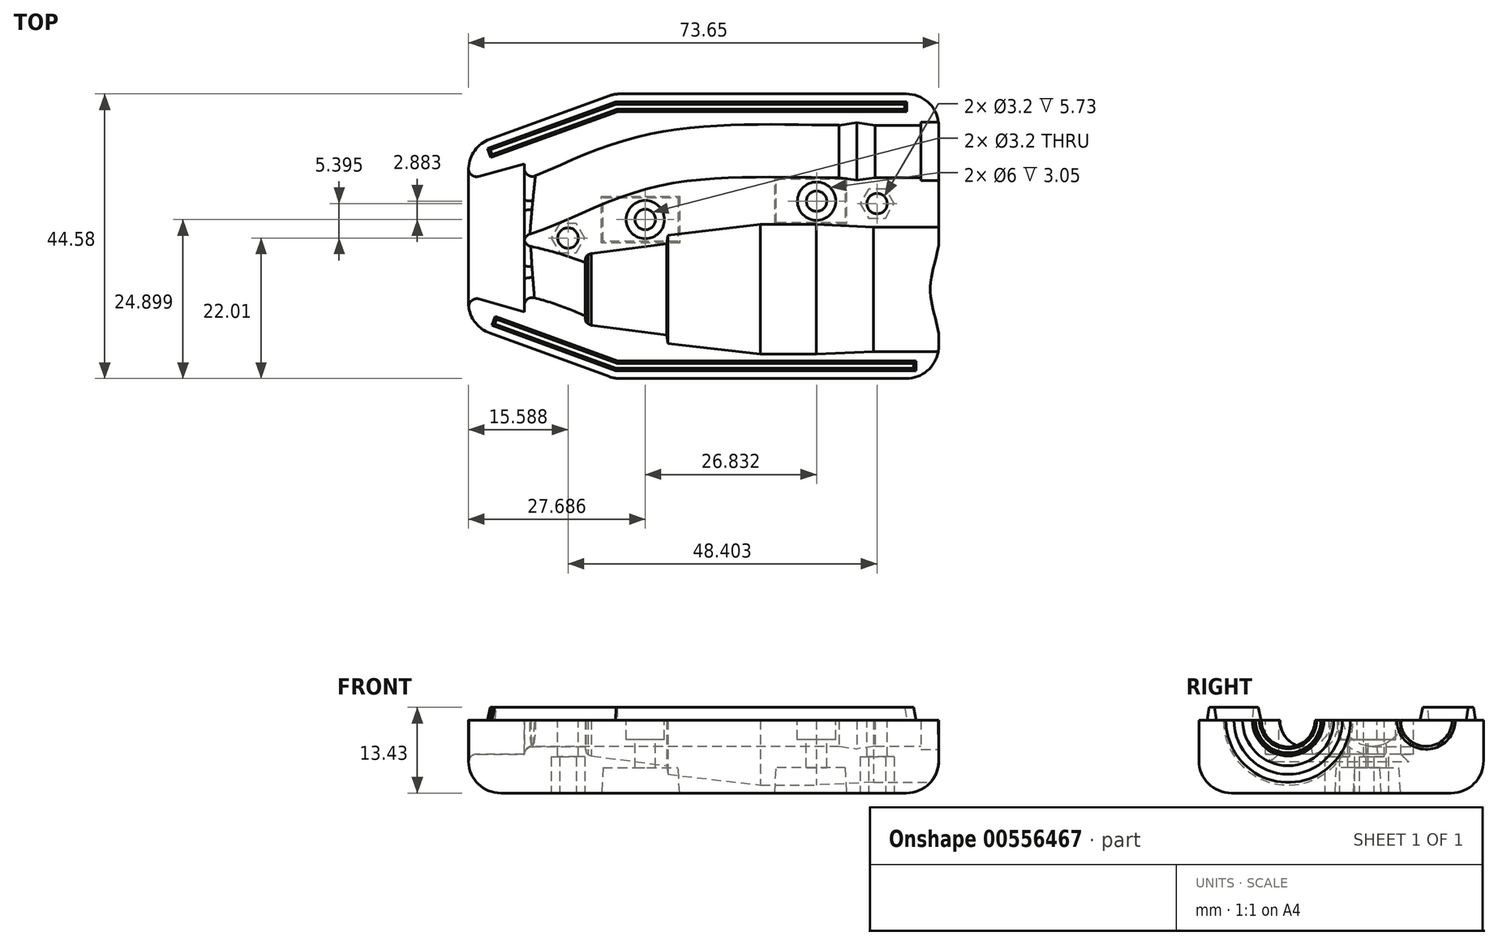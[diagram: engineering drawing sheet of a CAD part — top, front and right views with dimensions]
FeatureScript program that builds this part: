
annotation { "Feature Type Name" : "Feature", "Feature Type Description" : "" }
export const myFeature = defineFeature(function(context is Context, id is Id, definition is map)
    precondition{}
    {
        {
            var Q0;
            Q0=qCreatedBy(makeId("Top.planeOp"),FACE);
            var sketch = newSketch(context, id + "F0", { "sketchPlane" : qUnion([Q0])});
            skLineSegment(sketch, "E0", {"start": v(-29.16, 2.44) * mm, "end": v(45.25, 2.44) * mm});
            skLineSegment(sketch, "E1", {"start": v(45.25, 2.44) * mm, "end": v(45.25, -7.31) * mm});
            skLineSegment(sketch, "E2", {"start": v(45.25, -7.31) * mm, "end": v(33.01, -7.3) * mm});
            skLineSegment(sketch, "E3", {"start": v(33.01, -7.3) * mm, "end": v(31, -7.31) * mm});
            skLineSegment(sketch, "E4", {"start": v(31, -7.31) * mm, "end": v(16, -7.31) * mm});
            skLineSegment(sketch, "E5", {"start": v(16, -7.31) * mm, "end": v(7, -7.72) * mm});
            skLineSegment(sketch, "E6", {"start": v(7, -7.72) * mm, "end": v(-1.71, -7.72) * mm});
            skLineSegment(sketch, "E7", {"start": v(-1.71, -7.72) * mm, "end": v(-16.21, -6.04) * mm});
            skLineSegment(sketch, "E8", {"start": v(-16.21, -6.04) * mm, "end": v(-16.37, -4.7) * mm});
            skLineSegment(sketch, "E9", {"start": v(-16.37, -4.7) * mm, "end": v(-28.19, -3.17) * mm});
            skLineSegment(sketch, "E10", {"start": v(-28.19, -3.17) * mm, "end": v(-28.73, -2.96) * mm});
            skLineSegment(sketch, "E11", {"start": v(-28.73, -2.96) * mm, "end": v(-29.03, -2.68) * mm});
            skLineSegment(sketch, "E12", {"start": v(-29.03, -2.68) * mm, "end": v(-29.18, -2.06) * mm});
            skLineSegment(sketch, "E13", {"start": v(-29.18, -2.06) * mm, "end": v(-29.16, 2.44) * mm});
            skLineSegment(sketch, "E14.top", {"start": v(29.2, 18.83) * mm, "end": v(41.5, 18.83) * mm});
            skLineSegment(sketch, "E14.right", {"start": v(41.5, 24.03) * mm, "end": v(41.5, 18.83) * mm});
            skLineSegment(sketch, "E15", {"start": v(29.2, 19.46) * mm, "end": v(23.4, 19.46) * mm});
            skLineSegment(sketch, "E16", {"start": v(23.4, 19.46) * mm, "end": v(23.4, 24.03) * mm});
            skLineSegment(sketch, "E17", {"start": v(41.5, 24.03) * mm, "end": v(23.4, 24.03) * mm});
            skLineSegment(sketch, "E18", {"start": v(29.2, 18.83) * mm, "end": v(29.2, 19.46) * mm});
            skLineSegment(sketch, "E19.MirrorCS", {"start": v(-28.73, 7.85) * mm, "end": v(-29.03, 7.56) * mm});
            skLineSegment(sketch, "E20.MirrorCS", {"start": v(-29.03, 7.56) * mm, "end": v(-29.18, 6.94) * mm});
            skLineSegment(sketch, "E21.MirrorCS", {"start": v(33.01, 12.2) * mm, "end": v(31, 12.2) * mm});
            skLineSegment(sketch, "E22.MirrorCS", {"start": v(-28.19, 8.06) * mm, "end": v(-28.73, 7.85) * mm});
            skLineSegment(sketch, "E23.MirrorCS", {"start": v(-16.21, 10.93) * mm, "end": v(-16.37, 9.58) * mm});
            skLineSegment(sketch, "E24.MirrorCS", {"start": v(-16.37, 9.58) * mm, "end": v(-28.19, 8.06) * mm});
            skLineSegment(sketch, "E25.MirrorCS", {"start": v(7, 12.6) * mm, "end": v(-1.71, 12.6) * mm});
            skLineSegment(sketch, "E26.MirrorCS", {"start": v(45.25, 12.2) * mm, "end": v(33.01, 12.2) * mm});
            skLineSegment(sketch, "E27.MirrorCS", {"start": v(-1.71, 12.6) * mm, "end": v(-16.21, 10.93) * mm});
            skLineSegment(sketch, "E28.MirrorCS", {"start": v(16, 12.2) * mm, "end": v(7, 12.6) * mm});
            skLineSegment(sketch, "E29.MirrorCS", {"start": v(31, 12.2) * mm, "end": v(16, 12.2) * mm});
            skLineSegment(sketch, "E30.MirrorCS", {"start": v(45.25, 2.44) * mm, "end": v(45.25, 12.2) * mm});
            skLineSegment(sketch, "E31.MirrorCS", {"start": v(-29.18, 6.94) * mm, "end": v(-29.16, 2.44) * mm});
            skLineSegment(sketch, "E32", {"start": v(41.5, 20.03) * mm, "end": v(44.1, 20.03) * mm});
            skLineSegment(sketch, "E33", {"start": v(44.1, 20.03) * mm, "end": v(44.1, 24.03) * mm});
            skLineSegment(sketch, "E34", {"start": v(44.1, 24.03) * mm, "end": v(41.5, 24.03) * mm});
            skLineSegment(sketch, "E35", {"start": v(44.1, 20.03) * mm, "end": v(44.1, 19.46) * mm});
            skLineSegment(sketch, "E36", {"start": v(44.1, 19.46) * mm, "end": v(45.25, 19.46) * mm});
            skLineSegment(sketch, "E37", {"start": v(45.25, 19.46) * mm, "end": v(45.32, 24.03) * mm});
            skLineSegment(sketch, "E38", {"start": v(45.32, 24.03) * mm, "end": v(44.1, 24.03) * mm});
            skLineSegment(sketch, "E39", {"start": v(23.4, 24.03) * mm, "end": v(16.2, 24.03) * mm});
            skLineSegment(sketch, "E40", {"start": v(16.2, 24.03) * mm, "end": v(16.2, 19.93) * mm});
            skLineSegment(sketch, "E41", {"start": v(16.2, 19.93) * mm, "end": v(23.4, 19.93) * mm});
            skLineSegment(sketch, "E42", {"start": v(16.2, 19.93) * mm, "end": v(13.4, 19.53) * mm});
            skLineSegment(sketch, "E43", {"start": v(13.4, 19.53) * mm, "end": v(10.6, 19.93) * mm});
            skLineSegment(sketch, "E44", {"start": v(10.6, 19.93) * mm, "end": v(10.6, 24.03) * mm});
            skLineSegment(sketch, "E45", {"start": v(10.6, 24.03) * mm, "end": v(16.2, 24.03) * mm});
            skLineSegment(sketch, "E46.MirrorCS", {"start": v(44.1, 28.03) * mm, "end": v(44.1, 28.6) * mm});
            skLineSegment(sketch, "E47.MirrorCS", {"start": v(44.1, 28.6) * mm, "end": v(45.25, 28.6) * mm});
            skLineSegment(sketch, "E48.MirrorCS", {"start": v(29.2, 29.24) * mm, "end": v(29.2, 28.6) * mm});
            skLineSegment(sketch, "E49.MirrorCS", {"start": v(44.1, 28.03) * mm, "end": v(44.1, 24.03) * mm});
            skLineSegment(sketch, "E50.MirrorCS", {"start": v(16.2, 24.03) * mm, "end": v(16.2, 28.13) * mm});
            skLineSegment(sketch, "E51.MirrorCS", {"start": v(23.4, 28.6) * mm, "end": v(23.4, 24.03) * mm});
            skLineSegment(sketch, "E52.MirrorCS", {"start": v(10.6, 28.13) * mm, "end": v(10.6, 24.03) * mm});
            skLineSegment(sketch, "E53.MirrorCS", {"start": v(29.2, 28.6) * mm, "end": v(23.4, 28.6) * mm});
            skLineSegment(sketch, "E54.MirrorCS", {"start": v(41.5, 24.03) * mm, "end": v(41.5, 29.24) * mm});
            skLineSegment(sketch, "E55.MirrorCS", {"start": v(29.2, 29.24) * mm, "end": v(41.5, 29.24) * mm});
            skLineSegment(sketch, "E56.MirrorCS", {"start": v(45.25, 28.6) * mm, "end": v(45.32, 24.03) * mm});
            skLineSegment(sketch, "E57.MirrorCS", {"start": v(13.4, 28.53) * mm, "end": v(10.6, 28.13) * mm});
            skLineSegment(sketch, "E58.MirrorCS", {"start": v(41.5, 28.03) * mm, "end": v(44.1, 28.03) * mm});
            skLineSegment(sketch, "E59.MirrorCS", {"start": v(16.2, 28.13) * mm, "end": v(13.4, 28.53) * mm});
            skLineSegment(sketch, "E60.MirrorCS", {"start": v(16.2, 28.13) * mm, "end": v(23.4, 28.13) * mm});
            skSolve(sketch);
        }
        {
            var Q0;
            Q0=qCreatedBy(makeId("Top.planeOp"),FACE);
            var sketch = newSketch(context, id + "F1", { "sketchPlane" : qUnion([Q0])});
            skLineSegment(sketch, "E61.0", {"start": v(45.25, 2.44) * mm, "end": v(45.25, -7.31) * mm});
            skLineSegment(sketch, "E62", {"start": v(26.2, 33.05) * mm, "end": v(26.2, -11.53) * mm});
            skLineSegment(sketch, "E63", {"start": v(26.2, -11.53) * mm, "end": v(-24.6, -11.53) * mm});
            skLineSegment(sketch, "E64", {"start": v(-24.6, -11.53) * mm, "end": v(-47.46, -3.2) * mm});
            skLineSegment(sketch, "E65", {"start": v(-47.46, -3.2) * mm, "end": v(-47.46, 24.73) * mm});
            skLineSegment(sketch, "E66", {"start": v(-47.46, 24.73) * mm, "end": v(-24.6, 33.05) * mm});
            skLineSegment(sketch, "E67", {"start": v(-24.6, 33.05) * mm, "end": v(26.2, 33.05) * mm});
            skLineSegment(sketch, "E68.0", {"start": v(29.2, 29.24) * mm, "end": v(41.5, 29.24) * mm});
            skSolve(sketch);
        }
        {
            var Q0;
            Q0=qSketchRegion(id+"F1",true);
            extrude(context, id + "F2", {"entities" : qUnion([Q0]), "oppositeDirection" : true, "depth" : 11.43 * mm, "offsetDistance" : 25.4 * mm});
        }
        {
            var Q0;
            Q0=makeQuery(id+"F0.imprint","IMPRINT",FACE,{"disambiguationData":[TD([[makeQuery(id+"F0.imprint","IMPRINT",EDGE,{"derivedFrom":sQuery(id+"F0.wireOp",EDGE,"E0")}),-1.0]])]});
            var Q1;
            Q1=sQuery(id+"F0.wireOp",EDGE,"E0");
            revolve(context, id + "F3", {"operationType" : NewBodyOperationType.REMOVE, "entities" : qUnion([Q0]), "axis" : qUnion([Q1]), "revolveType" : RevolveType.FULL, "oppositeDirection" : true});
        }
        {
            var Q0;
            Q0=makeQuery(id+"F0.imprint","IMPRINT",FACE,{"disambiguationData":[TD([[makeQuery(id+"F0.imprint","IMPRINT",EDGE,{"derivedFrom":sQuery(id+"F0.wireOp",EDGE,"E14.top")}),1.0]])]});
            var Q1;
            Q1=makeQuery(id+"F0.imprint","IMPRINT",FACE,{"disambiguationData":[TD([[makeQuery(id+"F0.imprint","IMPRINT",EDGE,{"derivedFrom":sQuery(id+"F0.wireOp",EDGE,"E40")}),1.0]])]});
            var Q2;
            Q2=makeQuery(id+"F0.imprint","IMPRINT",FACE,{"disambiguationData":[TD([[makeQuery(id+"F0.imprint","IMPRINT",EDGE,{"derivedFrom":sQuery(id+"F0.wireOp",EDGE,"E40")}),-1.0]])]});
            var Q3;
            Q3=sQuery(id+"F0.wireOp",EDGE,"E17");
            revolve(context, id + "F4", {"operationType" : NewBodyOperationType.REMOVE, "entities" : qUnion([Q0, Q1, Q2]), "axis" : qUnion([Q3]), "revolveType" : RevolveType.FULL});
        }
        {
            var Q0;
            Q0=makeQuery(id+"F2.opExtrude","CAP_FACE",FACE,{"disambiguationData":[OSD([sQuery(id+"F1.wireOp",EDGE,"FN9DgEXL-DUnT-EqR8-ggIH-wTex11pTKOJ6"),sQuery(id+"F1.wireOp",EDGE,"Mmaicck8-LA38-ALDy-QV3c-pMFCgAv4KP83"),sQuery(id+"F1.wireOp",EDGE,"E62"),sQuery(id+"F1.wireOp",EDGE,"E63"),sQuery(id+"F1.wireOp",EDGE,"E64"),sQuery(id+"F1.wireOp",EDGE,"E65"),sQuery(id+"F1.wireOp",EDGE,"E66"),sQuery(id+"F1.wireOp",EDGE,"E67")])],"isStart":true});
            var sketch = newSketch(context, id + "F5", { "sketchPlane" : qUnion([Q0])});
            skLineSegment(sketch, "E69.0", {"start": v(-29.16, 2.44) * mm, "end": v(45.25, 2.44) * mm});
            skFitSpline(sketch, "E70", {"points": [v(-29.16, 2.44) * mm, v(-47.46, 6.7) * mm, v(-83.77, 9.93) * mm], "startDerivative": vector(-48.46, 20.5) * mm, "endDerivative": vector(-77.25, 2.74) * mm});
            skSolve(sketch);
        }
        {
            var Q0;
            Q0=sQuery(id+"F5.wireOp",VERTEX,"E70.0.internal");
            var Q1;
            Q1=sQuery(id+"F5.wireOp",EDGE,"E69.0");
            cPlane(context, id + "F6", {"entities" : qUnion([Q0, Q1]), "cplaneType" : CPlaneType.LINE_POINT, "offset" : 25.4 * mm, "width" : 152.4 * mm, "height" : 152.4 * mm});
        }
        {
            var Q0;
            Q0=qCreatedBy(id+"F6.planeOp",FACE);
            var sketch = newSketch(context, id + "F7", { "sketchPlane" : qUnion([Q0])});
            skCircle(sketch, "E71", {"center": v(2.44, 0) * mm, "radius": 4.2 * mm});
            skSolve(sketch);
        }
        {
            var Q0;
            Q0=qSketchRegion(id+"F7",true);
            var Q1;
            Q1=sQuery(id+"F5.wireOp",EDGE,"E70");
            sweep(context, id + "F8", {"operationType" : NewBodyOperationType.REMOVE, "profiles" : qUnion([Q0]), "path" : qUnion([Q1])});
        }
        {
            var Q0;
            Q0=sQuery(id+"F0.wireOp",VERTEX,"E45.start");
            var Q1;
            Q1=sQuery(id+"F0.wireOp",EDGE,"E45");
            cPlane(context, id + "F9", {"entities" : qUnion([Q0, Q1]), "cplaneType" : CPlaneType.LINE_POINT, "offset" : 25.4 * mm, "width" : 152.4 * mm, "height" : 152.4 * mm});
        }
        {
            var Q0;
            {var subQ0=sQuery(id+"F1.wireOp",EDGE,"E62");var subQ1=sQuery(id+"F1.wireOp",EDGE,"E65");var subQ2=sQuery(id+"F1.wireOp",EDGE,"E66");var subQ3=sQuery(id+"F1.wireOp",EDGE,"E67");Q0=makeQuery(id+"F8.boolean.opBoolean","SPLIT",FACE,{"disambiguationData":[TD([makeQuery(id+"F2.opExtrude","SWEPT_FACE",FACE,{"disambiguationData":[OSD([subQ2])]})])],"derivedFrom":makeQuery(id+"F2.opExtrude","CAP_FACE",FACE,{"disambiguationData":[OSD([subQ0,sQuery(id+"F1.wireOp",EDGE,"E63"),sQuery(id+"F1.wireOp",EDGE,"E64"),subQ1,subQ2,subQ3])],"isStart":true})});}
            var sketch = newSketch(context, id + "F10", { "sketchPlane" : qUnion([Q0])});
            skLineSegment(sketch, "E72.0", {"start": v(10.6, 24.03) * mm, "end": v(16.2, 24.03) * mm});
            skFitSpline(sketch, "E73", {"points": [v(10.6, 24.03) * mm, v(-17.54, 22.88) * mm, v(-35.92, 16.19) * mm, v(-61.27, 13.83) * mm], "startDerivative": vector(-66.57, 0.28) * mm, "endDerivative": vector(-121.3, 10.88) * mm});
            skSolve(sketch);
        }
        {
            var Q0;
            Q0=qCreatedBy(id+"F9.planeOp",FACE);
            var sketch = newSketch(context, id + "F11", { "sketchPlane" : qUnion([Q0])});
            skCircle(sketch, "E74", {"center": v(24.03, 0) * mm, "radius": 4.12 * mm});
            skSolve(sketch);
        }
        {
            var Q0;
            Q0=qSketchRegion(id+"F11",true);
            var Q1;
            Q1=sQuery(id+"F10.wireOp",EDGE,"E73");
            sweep(context, id + "F12", {"operationType" : NewBodyOperationType.REMOVE, "profiles" : qUnion([Q0]), "path" : qUnion([Q1])});
        }
        {
            var Q0;
            {var subQ4=sQuery(id+"F1.wireOp",EDGE,"E62");var subQ8=makeQuery(id+"F3.boolean.opBoolean","COPY",FACE,{"derivedFrom":makeQuery(id+"F3.opRevolve","SWEPT_FACE",FACE,{"disambiguationData":[OSD([sQuery(id+"F0.wireOp",EDGE,"E4")])]})});var subQ15=sQuery(id+"F1.wireOp",EDGE,"E65");var subQ16=sQuery(id+"F1.wireOp",EDGE,"E66");var subQ17=sQuery(id+"F1.wireOp",EDGE,"E67");Q0=makeQuery(id+"F12.boolean.opBoolean","SPLIT",FACE,{"disambiguationData":[TD([subQ8])],"derivedFrom":makeQuery(id+"F8.boolean.opBoolean","SPLIT",FACE,{"disambiguationData":[TD([makeQuery(id+"F2.opExtrude","SWEPT_FACE",FACE,{"disambiguationData":[OSD([subQ16])]})])],"derivedFrom":makeQuery(id+"F2.opExtrude","CAP_FACE",FACE,{"disambiguationData":[OSD([subQ4,sQuery(id+"F1.wireOp",EDGE,"E63"),sQuery(id+"F1.wireOp",EDGE,"E64"),subQ15,subQ16,subQ17])],"isStart":true})})});}
            var sketch = newSketch(context, id + "F13", { "sketchPlane" : qUnion([Q0])});
            skCircle(sketch, "E75", {"center": v(7.07, 16.25) * mm, "radius": 3 * mm});
            skCircle(sketch, "E76", {"center": v(-19.76, 13.37) * mm, "radius": 3 * mm});
            skSolve(sketch);
        }
        {
            var Q0;
            Q0 = qSketchRegion(id + "F13", true);
            extrude(context, id + "F14", {"entities" : qUnion([Q0]), "operationType" : NewBodyOperationType.REMOVE, "oppositeDirection" : true, "depth" : 3.05 * mm, "offsetDistance" : 25.4 * mm});
        }
        {
            var Q0;
            {var subQ4=sQuery(id+"F1.wireOp",EDGE,"E62");var subQ7=sQuery(id+"F1.wireOp",EDGE,"E65");var subQ8=makeQuery(id+"F2.opExtrude","SWEPT_FACE",FACE,{"disambiguationData":[OSD([subQ7])]});var subQ10=sQuery(id+"F1.wireOp",EDGE,"E66");var subQ11=makeQuery(id+"F2.opExtrude","SWEPT_FACE",FACE,{"disambiguationData":[OSD([subQ10])]});var subQ12=sQuery(id+"F1.wireOp",EDGE,"E67");Q0=makeQuery(id+"F12.boolean.opBoolean","SPLIT",FACE,{"disambiguationData":[TD([subQ8])],"derivedFrom":makeQuery(id+"F8.boolean.opBoolean","SPLIT",FACE,{"disambiguationData":[TD([subQ11])],"derivedFrom":makeQuery(id+"F2.opExtrude","CAP_FACE",FACE,{"disambiguationData":[OSD([subQ4,sQuery(id+"F1.wireOp",EDGE,"E63"),sQuery(id+"F1.wireOp",EDGE,"E64"),subQ7,subQ10,subQ12])],"isStart":true})})});}
            var sketch = newSketch(context, id + "F15", { "sketchPlane" : qUnion([Q0])});
            skLineSegment(sketch, "E77.0", {"start": v(-24.38, 31.8) * mm, "end": v(21.2, 31.8) * mm});
            skLineSegment(sketch, "E77.1", {"start": v(-44.47, 24.49) * mm, "end": v(-24.38, 31.8) * mm});
            skPoint(sketch, "E78", {"position": v(21.2, 31.8) * mm});
            skPoint(sketch, "E79", {"position": v(-44.47, 24.49) * mm});
            skLineSegment(sketch, "E80.0", {"start": v(-24.11, 30.3) * mm, "end": v(21.2, 30.3) * mm});
            skLineSegment(sketch, "E80.1", {"start": v(-43.95, 23.08) * mm, "end": v(-24.11, 30.3) * mm});
            skLineSegment(sketch, "E81", {"start": v(21.2, 30.3) * mm, "end": v(21.2, 31.8) * mm});
            skLineSegment(sketch, "E82", {"start": v(-44.47, 24.49) * mm, "end": v(-43.95, 23.08) * mm});
            skLineSegment(sketch, "E83.0", {"start": v(-24.38, -10.28) * mm, "end": v(-43.8, -3.21) * mm});
            skLineSegment(sketch, "E83.1", {"start": v(22.64, -10.28) * mm, "end": v(-24.38, -10.28) * mm});
            skPoint(sketch, "E84", {"position": v(22.64, -10.28) * mm});
            skPoint(sketch, "E85", {"position": v(-43.8, -3.21) * mm});
            skLineSegment(sketch, "E86.0", {"start": v(-24.11, -8.78) * mm, "end": v(-43.28, -1.8) * mm});
            skLineSegment(sketch, "E86.1", {"start": v(22.64, -8.78) * mm, "end": v(-24.11, -8.78) * mm});
            skLineSegment(sketch, "E87", {"start": v(22.64, -10.28) * mm, "end": v(22.64, -8.78) * mm});
            skLineSegment(sketch, "E88", {"start": v(-43.8, -3.21) * mm, "end": v(-43.28, -1.8) * mm});
            skSolve(sketch);
        }
        {
            var Q0;
            {var subQ4=sQuery(id+"F1.wireOp",EDGE,"E62");var subQ8=makeQuery(id+"F3.boolean.opBoolean","COPY",FACE,{"derivedFrom":makeQuery(id+"F3.opRevolve","SWEPT_FACE",FACE,{"disambiguationData":[OSD([sQuery(id+"F0.wireOp",EDGE,"E4")])]})});var subQ19=sQuery(id+"F1.wireOp",EDGE,"E65");var subQ20=sQuery(id+"F1.wireOp",EDGE,"E66");var subQ21=sQuery(id+"F1.wireOp",EDGE,"E67");Q0=makeQuery(id+"F12.boolean.opBoolean","SPLIT",FACE,{"disambiguationData":[TD([subQ8])],"derivedFrom":makeQuery(id+"F8.boolean.opBoolean","SPLIT",FACE,{"disambiguationData":[TD([makeQuery(id+"F2.opExtrude","SWEPT_FACE",FACE,{"disambiguationData":[OSD([subQ20])]})])],"derivedFrom":makeQuery(id+"F2.opExtrude","CAP_FACE",FACE,{"disambiguationData":[OSD([subQ4,sQuery(id+"F1.wireOp",EDGE,"E63"),sQuery(id+"F1.wireOp",EDGE,"E64"),subQ19,subQ20,subQ21])],"isStart":true})})});}
            var sketch = newSketch(context, id + "F16", { "sketchPlane" : qUnion([Q0])});
            skCircle(sketch, "E89", {"center": v(-19.76, 13.37) * mm, "radius": 1.6 * mm});
            skCircle(sketch, "E90", {"center": v(7.07, 16.25) * mm, "radius": 1.6 * mm});
            skSolve(sketch);
        }
        {
            var Q0;
            Q0=makeQuery(id+"F16.imprint","IMPRINT",FACE,{"disambiguationData":[TD([[makeQuery(id+"F16.imprint","IMPRINT",EDGE,{"derivedFrom":sQuery(id+"F16.wireOp",EDGE,"E89")}),1.0]])]});
            var Q1;
            Q1=makeQuery(id+"F16.imprint","IMPRINT",FACE,{"disambiguationData":[TD([[makeQuery(id+"F16.imprint","IMPRINT",EDGE,{"derivedFrom":sQuery(id+"F16.wireOp",EDGE,"E90")}),1.0]])]});
            extrude(context, id + "F17", {"entities" : qUnion([Q0, Q1]), "operationType" : NewBodyOperationType.REMOVE, "oppositeDirection" : true, "depth" : 25.4 * mm, "offsetDistance" : 25.4 * mm});
        }
        {
            var Q0;
            Q0 = qSketchRegion(id + "F15", true);
            extrude(context, id + "F18", {"entities" : qUnion([Q0]), "operationType" : NewBodyOperationType.ADD, "depth" : 2 * mm, "offsetDistance" : 25.4 * mm, "hasDraft" : true, "draftAngle" : 10 * degree, "draftPullDirection" : true});
        }
        {
            var Q0;
            Q0=makeQuery(id+"F2.opExtrude","CAP_FACE",FACE,{"disambiguationData":[OSD([sQuery(id+"F1.wireOp",EDGE,"E62"),sQuery(id+"F1.wireOp",EDGE,"E63"),sQuery(id+"F1.wireOp",EDGE,"E64"),sQuery(id+"F1.wireOp",EDGE,"E65"),sQuery(id+"F1.wireOp",EDGE,"E66"),sQuery(id+"F1.wireOp",EDGE,"E67")])],"isStart":false});
            var sketch = newSketch(context, id + "F19", { "sketchPlane" : qUnion([Q0])});
            skLineSegment(sketch, "E91.bottom", {"start": v(0.52, -12.67) * mm, "end": v(11.75, -12.67) * mm});
            skLineSegment(sketch, "E91.top", {"start": v(0.52, -19.97) * mm, "end": v(11.75, -19.97) * mm});
            skLineSegment(sketch, "E91.left", {"start": v(0.52, -12.67) * mm, "end": v(0.52, -19.97) * mm});
            skLineSegment(sketch, "E91.right", {"start": v(11.75, -12.67) * mm, "end": v(11.75, -19.97) * mm});
            skLineSegment(sketch, "E92.bottom", {"start": v(-14.4, -17.02) * mm, "end": v(-26.6, -17.02) * mm});
            skLineSegment(sketch, "E92.top", {"start": v(-14.4, -9.72) * mm, "end": v(-26.6, -9.72) * mm});
            skLineSegment(sketch, "E92.left", {"start": v(-14.4, -17.02) * mm, "end": v(-14.4, -9.72) * mm});
            skLineSegment(sketch, "E92.right", {"start": v(-26.6, -17.02) * mm, "end": v(-26.6, -9.72) * mm});
            skSolve(sketch);
        }
        {
            var Q0;
            Q0 = qSketchRegion(id + "F19", true);
            extrude(context, id + "F20", {"entities" : qUnion([Q0]), "operationType" : NewBodyOperationType.REMOVE, "oppositeDirection" : true, "depth" : 4 * mm, "offsetDistance" : 25.4 * mm, "hasDraft" : true, "draftAngle" : 3 * degree, "draftPullDirection" : true});
        }
        {
            var Q0;
            {var subQ4=sQuery(id+"F1.wireOp",EDGE,"E62");var subQ8=makeQuery(id+"F3.boolean.opBoolean","COPY",FACE,{"derivedFrom":makeQuery(id+"F3.opRevolve","SWEPT_FACE",FACE,{"disambiguationData":[OSD([sQuery(id+"F0.wireOp",EDGE,"E4")])]})});var subQ19=sQuery(id+"F1.wireOp",EDGE,"E65");var subQ20=sQuery(id+"F1.wireOp",EDGE,"E66");var subQ21=sQuery(id+"F1.wireOp",EDGE,"E67");Q0=makeQuery(id+"F12.boolean.opBoolean","SPLIT",FACE,{"disambiguationData":[TD([subQ8])],"derivedFrom":makeQuery(id+"F8.boolean.opBoolean","SPLIT",FACE,{"disambiguationData":[TD([makeQuery(id+"F2.opExtrude","SWEPT_FACE",FACE,{"disambiguationData":[OSD([subQ20])]})])],"derivedFrom":makeQuery(id+"F2.opExtrude","CAP_FACE",FACE,{"disambiguationData":[OSD([subQ4,sQuery(id+"F1.wireOp",EDGE,"E63"),sQuery(id+"F1.wireOp",EDGE,"E64"),subQ19,subQ20,subQ21])],"isStart":true})})});}
            var sketch = newSketch(context, id + "F21", { "sketchPlane" : qUnion([Q0])});
            skLineSegment(sketch, "E93", {"start": v(-48.77, 19.31) * mm, "end": v(-38.71, 22.1) * mm});
            skLineSegment(sketch, "E94", {"start": v(-38.71, 22.1) * mm, "end": v(-38.71, -1.1) * mm});
            skLineSegment(sketch, "E95", {"start": v(-38.71, -1.1) * mm, "end": v(-48.92, 1.83) * mm});
            skLineSegment(sketch, "E96", {"start": v(-48.92, 1.83) * mm, "end": v(-48.77, 19.31) * mm});
            skSolve(sketch);
        }
        {
            var Q0;
            Q0 = qSketchRegion(id + "F21", true);
            extrude(context, id + "F22", {"entities" : qUnion([Q0]), "operationType" : NewBodyOperationType.REMOVE, "oppositeDirection" : true, "depth" : 5.33 * mm, "offsetDistance" : 25.4 * mm});
        }
        {
            var Q0;
            Q0=makeQuery(id+"F2.opExtrude","SWEPT_EDGE",EDGE,{"disambiguationData":[OSD([sQuery(id+"F1.wireOp",EDGE,"E62"),sQuery(id+"F1.wireOp",EDGE,"E63")])]});
            var Q1;
            Q1=makeQuery(id+"F2.opExtrude","CAP_EDGE",EDGE,{"disambiguationData":[OSD([sQuery(id+"F1.wireOp",EDGE,"E63")])],"isStart":false});
            var Q2;
            Q2=makeQuery(id+"F2.opExtrude","CAP_EDGE",EDGE,{"disambiguationData":[OSD([sQuery(id+"F1.wireOp",EDGE,"E62")])],"isStart":false});
            var Q3;
            Q3=makeQuery(id+"F2.opExtrude","CAP_EDGE",EDGE,{"disambiguationData":[OSD([sQuery(id+"F1.wireOp",EDGE,"E64")])],"isStart":false});
            var Q4;
            Q4=makeQuery(id+"F2.opExtrude","SWEPT_EDGE",EDGE,{"disambiguationData":[OSD([sQuery(id+"F1.wireOp",EDGE,"E63"),sQuery(id+"F1.wireOp",EDGE,"E64")])]});
            var Q5;
            Q5=makeQuery(id+"F2.opExtrude","CAP_EDGE",EDGE,{"disambiguationData":[OSD([sQuery(id+"F1.wireOp",EDGE,"E65")])],"isStart":false});
            var Q6;
            Q6=makeQuery(id+"F2.opExtrude","SWEPT_EDGE",EDGE,{"disambiguationData":[OSD([sQuery(id+"F1.wireOp",EDGE,"E64"),sQuery(id+"F1.wireOp",EDGE,"E65")])]});
            var Q7;
            Q7=makeQuery(id+"F2.opExtrude","SWEPT_EDGE",EDGE,{"disambiguationData":[OSD([sQuery(id+"F1.wireOp",EDGE,"E65"),sQuery(id+"F1.wireOp",EDGE,"E66")])]});
            var Q8;
            Q8=makeQuery(id+"F2.opExtrude","CAP_EDGE",EDGE,{"disambiguationData":[OSD([sQuery(id+"F1.wireOp",EDGE,"E66")])],"isStart":false});
            var Q9;
            Q9=makeQuery(id+"F2.opExtrude","SWEPT_EDGE",EDGE,{"disambiguationData":[OSD([sQuery(id+"F1.wireOp",EDGE,"E66"),sQuery(id+"F1.wireOp",EDGE,"E67")])]});
            var Q10;
            Q10=makeQuery(id+"F2.opExtrude","CAP_EDGE",EDGE,{"disambiguationData":[OSD([sQuery(id+"F1.wireOp",EDGE,"E67")])],"isStart":false});
            var Q11;
            Q11=makeQuery(id+"F2.opExtrude","SWEPT_EDGE",EDGE,{"disambiguationData":[OSD([sQuery(id+"F1.wireOp",EDGE,"E62"),sQuery(id+"F1.wireOp",EDGE,"E67")])]});
            fillet(context, id + "F23", {"entities" : qUnion([Q0, Q1, Q2, Q3, Q4, Q5, Q6, Q7, Q8, Q9, Q10, Q11]), "radius" : 5.08 * mm, "tangentPropagation" : true, "allowEdgeOverflow" : false});
        }
        {
            var Q0;
            Q0=makeQuery(id+"F22.boolean.opBoolean","INTERSECT",EDGE,{"derivedFrom":[makeQuery(id+"F12.boolean.opBoolean","COPY",FACE,{"derivedFrom":makeQuery(id+"F12.opSweep","SWEPT_FACE",FACE,{"disambiguationData":[OSD([sQuery(id+"F10.wireOp",EDGE,"E73"),sQuery(id+"F11.wireOp",EDGE,"E74")])]})}),makeQuery(id+"F22.opExtrude","SWEPT_FACE",FACE,{"disambiguationData":[OSD([sQuery(id+"F21.wireOp",EDGE,"E94")])]})]});
            var Q1;
            Q1=makeQuery(id+"F22.boolean.opBoolean","INTERSECT",EDGE,{"derivedFrom":[makeQuery(id+"F8.boolean.opBoolean","COPY",FACE,{"derivedFrom":makeQuery(id+"F8.opSweep","SWEPT_FACE",FACE,{"disambiguationData":[OSD([sQuery(id+"F5.wireOp",EDGE,"E70"),sQuery(id+"F7.wireOp",EDGE,"E71")])]})}),makeQuery(id+"F22.opExtrude","SWEPT_FACE",FACE,{"disambiguationData":[OSD([sQuery(id+"F21.wireOp",EDGE,"E94")])]})]});
            var Q2;
            Q2=makeQuery(id+"F22.boolean.opBoolean","INTERSECT",EDGE,{"derivedFrom":[makeQuery(id+"F2.opExtrude","SWEPT_FACE",FACE,{"disambiguationData":[OSD([sQuery(id+"F1.wireOp",EDGE,"E65")])]}),makeQuery(id+"F22.opExtrude","CAP_FACE",FACE,{"disambiguationData":[OSD([sQuery(id+"F21.wireOp",EDGE,"E93"),sQuery(id+"F21.wireOp",EDGE,"E94"),sQuery(id+"F21.wireOp",EDGE,"E95"),sQuery(id+"F21.wireOp",EDGE,"E96")])],"isStart":false})]});
            fillet(context, id + "F24", {"entities" : qUnion([Q0, Q1, Q2]), "radius" : 1.27 * mm, "tangentPropagation" : true, "allowEdgeOverflow" : false});
        }
        {
            var Q0;
            Q0=makeQuery(id+"F22.boolean.opBoolean","INTERSECT",EDGE,{"derivedFrom":[makeQuery(id+"F2.opExtrude","SWEPT_FACE",FACE,{"disambiguationData":[OSD([sQuery(id+"F1.wireOp",EDGE,"E65")])]}),makeQuery(id+"F22.opExtrude","SWEPT_FACE",FACE,{"disambiguationData":[OSD([sQuery(id+"F21.wireOp",EDGE,"E93")])]})]});
            var Q1;
            Q1=makeQuery(id+"F22.boolean.opBoolean","INTERSECT",EDGE,{"derivedFrom":[makeQuery(id+"F2.opExtrude","SWEPT_FACE",FACE,{"disambiguationData":[OSD([sQuery(id+"F1.wireOp",EDGE,"E65")])]}),makeQuery(id+"F22.opExtrude","SWEPT_FACE",FACE,{"disambiguationData":[OSD([sQuery(id+"F21.wireOp",EDGE,"E95")])]})]});
            fillet(context, id + "F25", {"entities" : qUnion([Q0, Q1]), "radius" : 1.27 * mm, "tangentPropagation" : true, "allowEdgeOverflow" : false});
        }
        {
            var Q0;
            {var subQ4=sQuery(id+"F1.wireOp",EDGE,"E62");var subQ8=makeQuery(id+"F3.boolean.opBoolean","COPY",FACE,{"derivedFrom":makeQuery(id+"F3.opRevolve","SWEPT_FACE",FACE,{"disambiguationData":[OSD([sQuery(id+"F0.wireOp",EDGE,"E4")])]})});var subQ19=sQuery(id+"F1.wireOp",EDGE,"E65");var subQ20=sQuery(id+"F1.wireOp",EDGE,"E66");var subQ21=sQuery(id+"F1.wireOp",EDGE,"E67");Q0=makeQuery(id+"F12.boolean.opBoolean","SPLIT",FACE,{"disambiguationData":[TD([subQ8])],"derivedFrom":makeQuery(id+"F8.boolean.opBoolean","SPLIT",FACE,{"disambiguationData":[TD([makeQuery(id+"F2.opExtrude","SWEPT_FACE",FACE,{"disambiguationData":[OSD([subQ20])]})])],"derivedFrom":makeQuery(id+"F2.opExtrude","CAP_FACE",FACE,{"disambiguationData":[OSD([subQ4,sQuery(id+"F1.wireOp",EDGE,"E63"),sQuery(id+"F1.wireOp",EDGE,"E64"),subQ19,subQ20,subQ21])],"isStart":true})})});}
            var sketch = newSketch(context, id + "F26", { "sketchPlane" : qUnion([Q0])});
            skCircle(sketch, "E97", {"center": v(-31.86, 10.48) * mm, "radius": 1.6 * mm});
            skCircle(sketch, "E98", {"center": v(16.54, 15.88) * mm, "radius": 1.6 * mm});
            skSolve(sketch);
        }
        {
            var Q0;
            Q0 = qSketchRegion(id + "F26", true);
            extrude(context, id + "F27", {"entities" : qUnion([Q0]), "operationType" : NewBodyOperationType.REMOVE, "oppositeDirection" : true, "depth" : 25.4 * mm, "offsetDistance" : 25.4 * mm});
        }
        {
            var Q0;
            Q0=makeQuery(id+"F2.opExtrude","CAP_FACE",FACE,{"disambiguationData":[OSD([sQuery(id+"F1.wireOp",EDGE,"E62"),sQuery(id+"F1.wireOp",EDGE,"E63"),sQuery(id+"F1.wireOp",EDGE,"E64"),sQuery(id+"F1.wireOp",EDGE,"E65"),sQuery(id+"F1.wireOp",EDGE,"E66"),sQuery(id+"F1.wireOp",EDGE,"E67")])],"isStart":false});
            var sketch = newSketch(context, id + "F28", { "sketchPlane" : qUnion([Q0])});
            skCircle(sketch, "E99.0", {"center": v(-31.86, -10.48) * mm, "radius": 1.6 * mm});
            skCircle(sketch, "E100.0", {"center": v(16.54, -15.88) * mm, "radius": 1.6 * mm});
            skCircle(sketch, "E101.cCircle", {"center": v(-31.86, -10.48) * mm, "radius": 2.65 * mm, "construction": true});
            skLineSegment(sketch, "E101.0", {"start": v(-29.21, -10.48) * mm, "end": v(-30.54, -12.78) * mm});
            skLineSegment(sketch, "E101.1", {"start": v(-30.54, -12.78) * mm, "end": v(-33.19, -12.78) * mm});
            skLineSegment(sketch, "E101.2", {"start": v(-33.19, -12.78) * mm, "end": v(-34.51, -10.48) * mm});
            skLineSegment(sketch, "E101.3", {"start": v(-34.51, -10.48) * mm, "end": v(-33.19, -8.19) * mm});
            skLineSegment(sketch, "E101.4", {"start": v(-33.19, -8.19) * mm, "end": v(-30.54, -8.19) * mm});
            skLineSegment(sketch, "E101.5", {"start": v(-30.54, -8.19) * mm, "end": v(-29.21, -10.48) * mm});
            skCircle(sketch, "E102.cCircle", {"center": v(16.54, -15.88) * mm, "radius": 2.65 * mm, "construction": true});
            skLineSegment(sketch, "E102.0", {"start": v(19.2, -15.88) * mm, "end": v(17.87, -18.17) * mm});
            skLineSegment(sketch, "E102.1", {"start": v(17.87, -18.17) * mm, "end": v(15.22, -18.17) * mm});
            skLineSegment(sketch, "E102.2", {"start": v(15.22, -18.17) * mm, "end": v(13.9, -15.88) * mm});
            skLineSegment(sketch, "E102.3", {"start": v(13.9, -15.88) * mm, "end": v(15.22, -13.58) * mm});
            skLineSegment(sketch, "E102.4", {"start": v(15.22, -13.58) * mm, "end": v(17.87, -13.58) * mm});
            skLineSegment(sketch, "E102.5", {"start": v(17.87, -13.58) * mm, "end": v(19.2, -15.88) * mm});
            skSolve(sketch);
        }
        {
            var Q0;
            Q0 = qSketchRegion(id + "F28", true);
            extrude(context, id + "F29", {"entities" : qUnion([Q0]), "operationType" : NewBodyOperationType.REMOVE, "oppositeDirection" : true, "depth" : 5.7 * mm, "offsetDistance" : 25.4 * mm});
        }
    });
